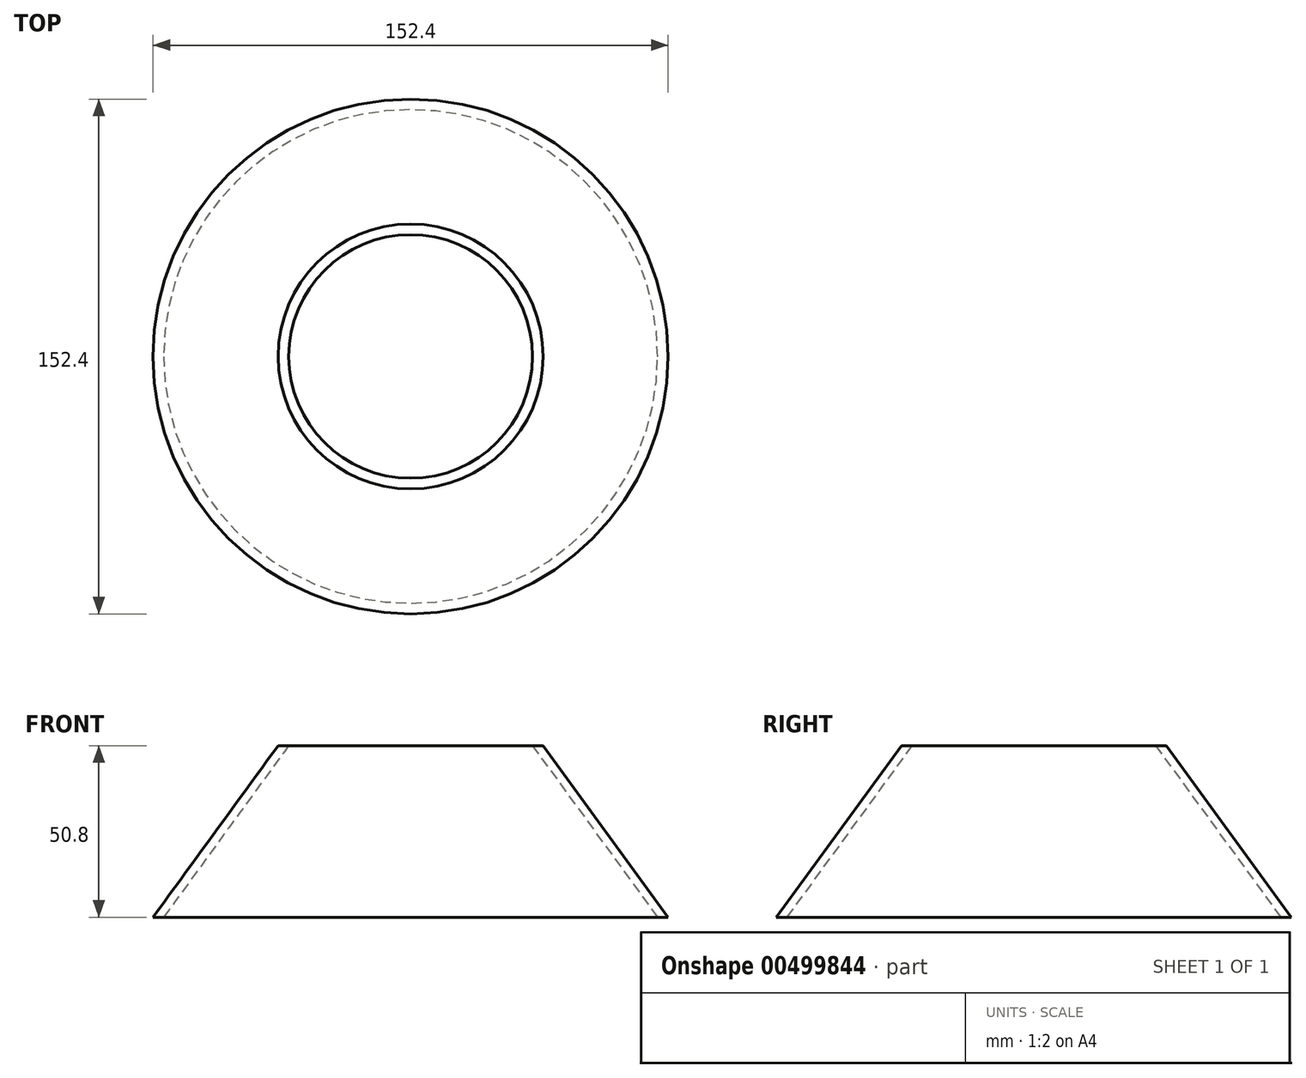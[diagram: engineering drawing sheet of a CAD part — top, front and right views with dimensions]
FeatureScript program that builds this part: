
annotation { "Feature Type Name" : "Feature", "Feature Type Description" : "" }
export const myFeature = defineFeature(function(context is Context, id is Id, definition is map)
    precondition{}
    {
        {
            var Q0;
            Q0=qCreatedBy(makeId("Front.planeOp"),FACE);
            var sketch = newSketch(context, id + "F0", { "sketchPlane" : qUnion([Q0])});
            skLineSegment(sketch, "E0", {"start": v(0, 0) * mm, "end": v(0, 50.8) * mm});
            skLineSegment(sketch, "E1", {"start": v(0, 50.8) * mm, "end": v(39.2, 50.8) * mm});
            skLineSegment(sketch, "E2", {"start": v(39.2, 50.8) * mm, "end": v(76.2, 0) * mm});
            skLineSegment(sketch, "E3", {"start": v(76.2, 0) * mm, "end": v(0, 0) * mm});
            skSolve(sketch);
        }
        {
            var Q0;
            Q0=makeQuery(id+"F0.imprint","IMPRINT",FACE,{"disambiguationData":[TD([[makeQuery(id+"F0.imprint","IMPRINT",EDGE,{"derivedFrom":sQuery(id+"F0.wireOp",EDGE,"E0")}),-1.0]])]});
            var Q1;
            Q1=sQuery(id+"F0.wireOp",EDGE,"E0");
            revolve(context, id + "F1", {"entities" : qUnion([Q0]), "axis" : qUnion([Q1]), "revolveType" : RevolveType.FULL});
        }
        {
            var Q0;
            Q0=makeQuery(id+"F1.opRevolve","SWEPT_FACE",FACE,{"disambiguationData":[OSD([sQuery(id+"F0.wireOp",EDGE,"E3")])]});
            var Q1;
            Q1=makeQuery(id+"F1.opRevolve","SWEPT_FACE",FACE,{"disambiguationData":[OSD([sQuery(id+"F0.wireOp",EDGE,"E1")])]});
            shell(context, id + "F2", {"entities" : qUnion([Q0, Q1]), "thickness" : 2.54 * mm});
        }
    });
